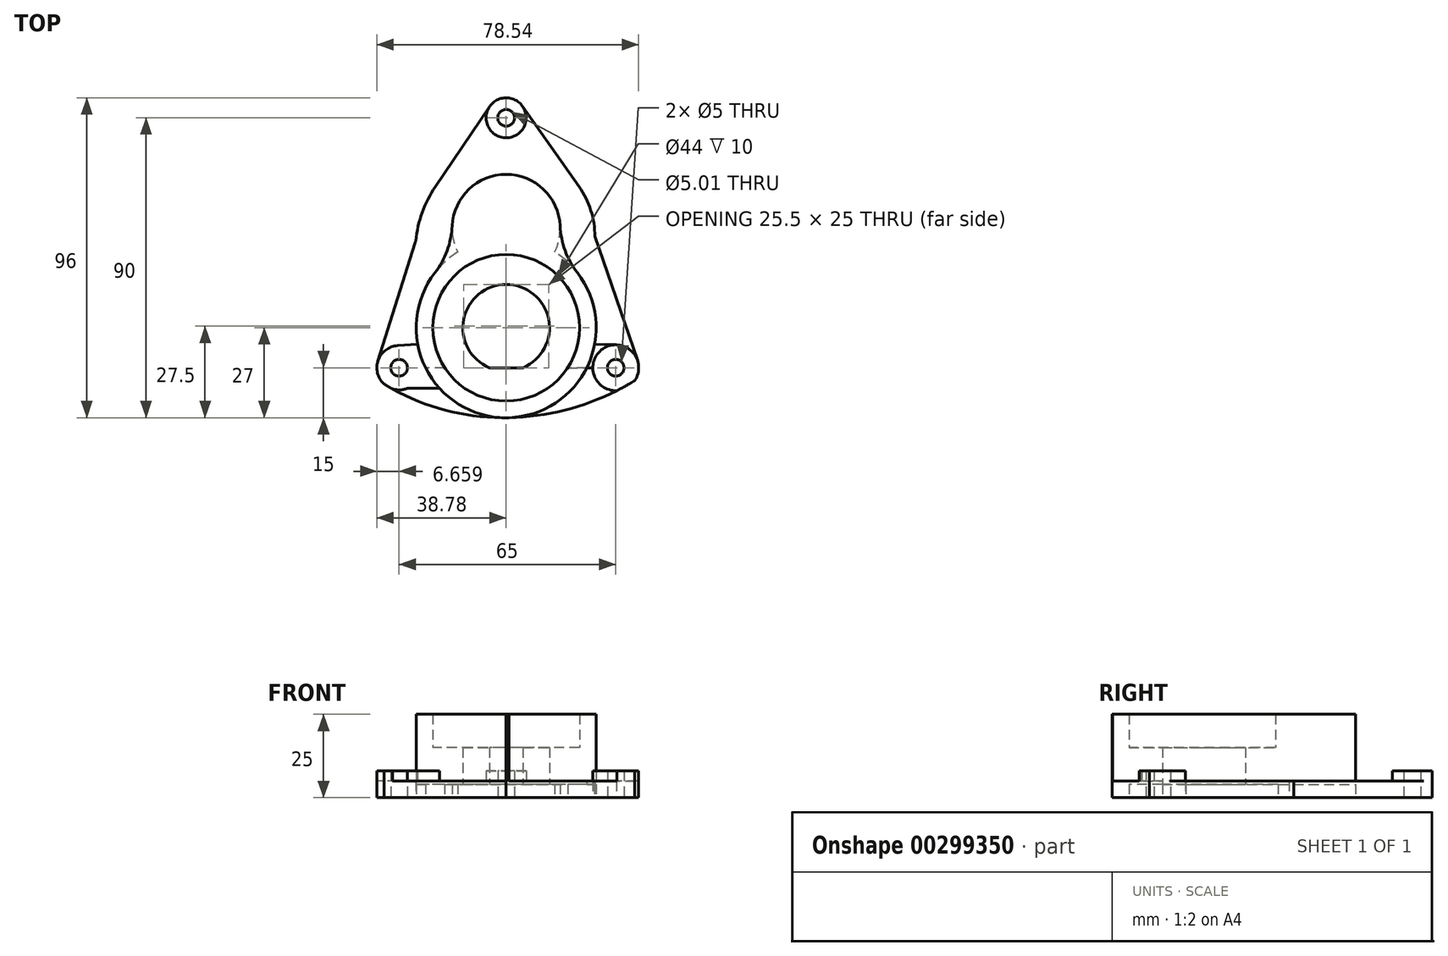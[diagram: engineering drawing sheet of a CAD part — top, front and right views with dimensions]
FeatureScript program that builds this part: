
annotation { "Feature Type Name" : "Feature", "Feature Type Description" : "" }
export const myFeature = defineFeature(function(context is Context, id is Id, definition is map)
    precondition{}
    {
        {
            var Q0;
            Q0=qCreatedBy(makeId("Top.planeOp"),FACE);
            var sketch = newSketch(context, id + "F0", { "sketchPlane" : qUnion([Q0])});
            skCircle(sketch, "E0", {"center": v(0, 0) * mm, "radius": 13 * mm});
            skCircle(sketch, "E1", {"center": v(0, 0) * mm, "radius": 22 * mm});
            skCircle(sketch, "E2", {"center": v(0, 0) * mm, "radius": 27 * mm});
            skLineSegment(sketch, "E3", {"start": v(-99.8, -12) * mm, "end": v(99.48, -12) * mm});
            skCircle(sketch, "E4", {"center": v(32.88, -12) * mm, "radius": 2.5 * mm});
            skCircle(sketch, "E5", {"center": v(32.88, -12) * mm, "radius": 6.88 * mm});
            skCircle(sketch, "E6", {"center": v(-32.12, -12) * mm, "radius": 2.5 * mm});
            skCircle(sketch, "E7", {"center": v(-32.12, -12) * mm, "radius": 6.66 * mm});
            skCircle(sketch, "E8", {"center": v(0, 29.79) * mm, "radius": 11.21 * mm});
            skArc(sketch, "E9", {"start": v(14.59, 22.72) * mm, "mid": v(0, 46) * mm, "end": v(-14.59, 22.72) * mm});
            skCircle(sketch, "E10", {"center": v(0, 63) * mm, "radius": 6 * mm});
            skCircle(sketch, "E11", {"center": v(0, 63) * mm, "radius": 2.5 * mm});
            skLineSegment(sketch, "E12", {"start": v(-32.55, -5.36) * mm, "end": v(-26.54, -4.97) * mm});
            skLineSegment(sketch, "E13", {"start": v(-34.56, -18.2) * mm, "end": v(-19.95, -18.2) * mm});
            skLineSegment(sketch, "E14", {"start": v(33.04, -5.12) * mm, "end": v(26.54, -4.97) * mm});
            skLineSegment(sketch, "E15", {"start": v(33.32, -18.87) * mm, "end": v(19.62, -18.55) * mm});
            skLineSegment(sketch, "E16", {"start": v(-27.35, 25.47) * mm, "end": v(-39.1, -12) * mm});
            skLineSegment(sketch, "E17", {"start": v(26.61, 27.38) * mm, "end": v(40.16, -12) * mm});
            skArc(sketch, "E18", {"start": v(0, -27) * mm, "mid": v(20.05, -24.05) * mm, "end": v(38.58, -15.85) * mm});
            skArc(sketch, "E19", {"start": v(-36.68, -16.85) * mm, "mid": v(-19.05, -24.5) * mm, "end": v(0, -27) * mm});
            skLineSegment(sketch, "E20", {"start": v(0, -27) * mm, "end": v(-95.56, -27) * mm});
            skLineSegment(sketch, "E21", {"start": v(-21.25, 42.32) * mm, "end": v(-4.97, 66.36) * mm});
            skLineSegment(sketch, "E22", {"start": v(21.9, 42.32) * mm, "end": v(4.9, 66.45) * mm});
            skLineSegment(sketch, "E23", {"start": v(4.1, 45.47) * mm, "end": v(2.99, 57.8) * mm});
            skLineSegment(sketch, "E24", {"start": v(-4.1, 45.47) * mm, "end": v(-2.99, 57.8) * mm});
            skPoint(sketch, "E25.visualSharp", {"position": v(-26.96, 26.7) * mm});
            skArc(sketch, "E25.filletArc", {"start": v(-27.1, 26.1) * mm, "mid": v(-27.24, 25.78) * mm, "end": v(-27.35, 25.47) * mm});
            skPoint(sketch, "E26.visualSharp", {"position": v(26.2, 28.55) * mm});
            skArc(sketch, "E27", {"start": v(-21.25, 42.32) * mm, "mid": v(-25.2, 34.57) * mm, "end": v(-27.1, 26.1) * mm});
            skArc(sketch, "E28", {"start": v(21.9, 42.32) * mm, "mid": v(25.41, 35.21) * mm, "end": v(26.61, 27.38) * mm});
            skSolve(sketch);
        }
        {
            var Q0;
            {var subQ1=sQuery(id+"F0.wireOp",EDGE,"E2");var subQ4=sQuery(id+"F0.wireOp",EDGE,"E9");var subQ6=makeQuery(id+"F0.imprint","INTERSECT",VERTEX,{"disambiguationData":[OD(0.0)],"derivedFrom":[subQ1,subQ4]});Q0=makeQuery(id+"F0.imprint","IMPRINT",FACE,{"disambiguationData":[TD([[makeQuery(id+"F0.imprint","IMPRINT",EDGE,{"disambiguationData":[TD([[subQ6,-1.0]])],"derivedFrom":subQ1}),-1.0]])]});}
            var Q1;
            {var subQ1=sQuery(id+"F0.wireOp",EDGE,"E1");var subQ6=sQuery(id+"F0.wireOp",EDGE,"E8");var subQ7=makeQuery(id+"F0.imprint","INTERSECT",VERTEX,{"disambiguationData":[OD(1.0)],"derivedFrom":[subQ1,subQ6]});Q1=makeQuery(id+"F0.imprint","IMPRINT",FACE,{"disambiguationData":[TD([[makeQuery(id+"F0.imprint","IMPRINT",EDGE,{"disambiguationData":[TD([[subQ7,1.0]])],"derivedFrom":subQ1}),-1.0]])]});}
            var Q2;
            {var subQ5=sQuery(id+"F0.wireOp",EDGE,"E8");var subQ7=sQuery(id+"F0.wireOp",EDGE,"E1");var subQ8=makeQuery(id+"F0.imprint","INTERSECT",VERTEX,{"disambiguationData":[OD(0.0)],"derivedFrom":[subQ7,subQ5]});Q2=makeQuery(id+"F0.imprint","IMPRINT",FACE,{"disambiguationData":[TD([[makeQuery(id+"F0.imprint","IMPRINT",EDGE,{"disambiguationData":[TD([[subQ8,-1.0]])],"derivedFrom":subQ7}),-1.0]])]});}
            var Q3;
            {var subQ4=sQuery(id+"F0.wireOp",EDGE,"E3");var subQ6=sQuery(id+"F0.wireOp",EDGE,"E1");var subQ7=makeQuery(id+"F0.imprint","INTERSECT",VERTEX,{"disambiguationData":[OD(0.0)],"derivedFrom":[subQ6,subQ4]});Q3=makeQuery(id+"F0.imprint","IMPRINT",FACE,{"disambiguationData":[TD([[makeQuery(id+"F0.imprint","IMPRINT",EDGE,{"disambiguationData":[TD([[subQ7,-1.0]])],"derivedFrom":subQ6}),-1.0]])]});}
            extrude(context, id + "F1", {"entities" : qUnion([Q0, Q1, Q2, Q3]), "depth" : 25 * mm});
        }
        {
            var Q0;
            {var subQ3=sQuery(id+"F0.wireOp",EDGE,"E3");var subQ5=sQuery(id+"F0.wireOp",EDGE,"E0");var subQ6=makeQuery(id+"F0.imprint","INTERSECT",VERTEX,{"disambiguationData":[OD(0.0)],"derivedFrom":[subQ5,subQ3]});Q0=makeQuery(id+"F0.imprint","IMPRINT",FACE,{"disambiguationData":[TD([[makeQuery(id+"F0.imprint","IMPRINT",EDGE,{"disambiguationData":[TD([[subQ6,1.0]])],"derivedFrom":subQ5}),-1.0]])]});}
            var Q1;
            {var subQ0=sQuery(id+"F0.wireOp",EDGE,"E3");var subQ1=sQuery(id+"F0.wireOp",EDGE,"E0");var subQ2=makeQuery(id+"F0.imprint","INTERSECT",VERTEX,{"disambiguationData":[OD(0.0)],"derivedFrom":[subQ1,subQ0]});Q1=makeQuery(id+"F0.imprint","IMPRINT",FACE,{"disambiguationData":[TD([[makeQuery(id+"F0.imprint","IMPRINT",EDGE,{"disambiguationData":[TD([[subQ2,1.0]])],"derivedFrom":subQ1}),1.0]])]});}
            var Q2;
            {var subQ0=sQuery(id+"F0.wireOp",EDGE,"E3");var subQ1=sQuery(id+"F0.wireOp",EDGE,"E0");var subQ2=makeQuery(id+"F0.imprint","INTERSECT",VERTEX,{"disambiguationData":[OD(0.0)],"derivedFrom":[subQ1,subQ0]});Q2=makeQuery(id+"F0.imprint","IMPRINT",FACE,{"disambiguationData":[TD([[makeQuery(id+"F0.imprint","IMPRINT",EDGE,{"disambiguationData":[TD([[subQ2,-1.0]])],"derivedFrom":subQ1}),-1.0]])]});}
            var Q3;
            {var subQ0=sQuery(id+"F0.wireOp",EDGE,"E8");var subQ1=sQuery(id+"F0.wireOp",EDGE,"E1");var subQ2=makeQuery(id+"F0.imprint","INTERSECT",VERTEX,{"disambiguationData":[OD(0.0)],"derivedFrom":[subQ1,subQ0]});Q3=makeQuery(id+"F0.imprint","IMPRINT",FACE,{"disambiguationData":[TD([[makeQuery(id+"F0.imprint","IMPRINT",EDGE,{"disambiguationData":[TD([[subQ2,1.0]])],"derivedFrom":subQ1}),1.0]])]});}
            var Q4;
            {var subQ0=sQuery(id+"F0.wireOp",EDGE,"E3");var subQ1=sQuery(id+"F0.wireOp",EDGE,"E0");var subQ2=makeQuery(id+"F0.imprint","INTERSECT",VERTEX,{"disambiguationData":[OD(0.0)],"derivedFrom":[subQ1,subQ0]});Q4=makeQuery(id+"F0.imprint","IMPRINT",FACE,{"disambiguationData":[TD([[makeQuery(id+"F0.imprint","IMPRINT",EDGE,{"disambiguationData":[TD([[subQ2,-1.0]])],"derivedFrom":subQ1}),1.0]])]});}
            extrude(context, id + "F2", {"entities" : qUnion([Q0, Q1, Q2, Q3, Q4]), "operationType" : NewBodyOperationType.ADD, "depth" : 15 * mm});
        }
        {
            var Q0;
            {var subQ0=sQuery(id+"F0.wireOp",EDGE,"E8");var subQ1=sQuery(id+"F0.wireOp",EDGE,"E2");var subQ2=makeQuery(id+"F0.imprint","INTERSECT",VERTEX,{"disambiguationData":[OD(0.0)],"derivedFrom":[subQ1,subQ0]});Q0=makeQuery(id+"F0.imprint","IMPRINT",FACE,{"disambiguationData":[TD([[makeQuery(id+"F0.imprint","IMPRINT",EDGE,{"disambiguationData":[TD([[subQ2,-1.0]])],"derivedFrom":subQ1}),-1.0]])]});}
            var Q1;
            {var subQ0=sQuery(id+"F0.wireOp",EDGE,"E8");var subQ1=sQuery(id+"F0.wireOp",EDGE,"E1");var subQ2=makeQuery(id+"F0.imprint","INTERSECT",VERTEX,{"disambiguationData":[OD(0.0)],"derivedFrom":[subQ1,subQ0]});Q1=makeQuery(id+"F0.imprint","IMPRINT",FACE,{"disambiguationData":[TD([[makeQuery(id+"F0.imprint","IMPRINT",EDGE,{"disambiguationData":[TD([[subQ2,1.0]])],"derivedFrom":subQ1}),-1.0]])]});}
            extrude(context, id + "F3", {"entities" : qUnion([Q0, Q1]), "operationType" : NewBodyOperationType.ADD, "depth" : 25 * mm});
        }
        {
            var Q0;
            {var subQ6=sQuery(id+"F0.wireOp",EDGE,"E12");Q0=makeQuery(id+"F0.imprint","IMPRINT",FACE,{"disambiguationData":[TD([[makeQuery(id+"F0.imprint","IMPRINT",EDGE,{"derivedFrom":subQ6}),1.0]])]});}
            var Q1;
            {var subQ0=sQuery(id+"F0.wireOp",EDGE,"E12");Q1=makeQuery(id+"F0.imprint","IMPRINT",FACE,{"disambiguationData":[TD([[makeQuery(id+"F0.imprint","IMPRINT",EDGE,{"derivedFrom":subQ0}),-1.0]])]});}
            var Q2;
            {var subQ0=sQuery(id+"F0.wireOp",EDGE,"E13");var subQ1=sQuery(id+"F0.wireOp",EDGE,"E2");var subQ2=makeQuery(id+"F0.imprint","INTERSECT",VERTEX,{"derivedFrom":[subQ1,subQ0]});Q2=makeQuery(id+"F0.imprint","IMPRINT",FACE,{"disambiguationData":[TD([[makeQuery(id+"F0.imprint","IMPRINT",EDGE,{"disambiguationData":[TD([[subQ2,1.0]])],"derivedFrom":subQ1}),-1.0]])]});}
            var Q3;
            {var subQ1=sQuery(id+"F0.wireOp",EDGE,"E19");var subQ3=sQuery(id+"F0.wireOp",EDGE,"E7");var subQ4=makeQuery(id+"F0.imprint","INTERSECT",VERTEX,{"disambiguationData":[OD(1.0)],"derivedFrom":[subQ3,subQ1]});Q3=makeQuery(id+"F0.imprint","IMPRINT",FACE,{"disambiguationData":[TD([[makeQuery(id+"F0.imprint","IMPRINT",EDGE,{"disambiguationData":[TD([[subQ4,-1.0]])],"derivedFrom":subQ3}),-1.0]])]});}
            var Q4;
            {var subQ0=sQuery(id+"F0.wireOp",EDGE,"E15");var subQ4=sQuery(id+"F0.wireOp",EDGE,"E2");var subQ5=makeQuery(id+"F0.imprint","INTERSECT",VERTEX,{"derivedFrom":[subQ4,subQ0]});Q4=makeQuery(id+"F0.imprint","IMPRINT",FACE,{"disambiguationData":[TD([[makeQuery(id+"F0.imprint","IMPRINT",EDGE,{"disambiguationData":[TD([[subQ5,1.0]])],"derivedFrom":subQ4}),-1.0]])]});}
            var Q5;
            {var subQ0=sQuery(id+"F0.wireOp",EDGE,"E15");var subQ1=sQuery(id+"F0.wireOp",EDGE,"E2");var subQ2=makeQuery(id+"F0.imprint","INTERSECT",VERTEX,{"derivedFrom":[subQ1,subQ0]});Q5=makeQuery(id+"F0.imprint","IMPRINT",FACE,{"disambiguationData":[TD([[makeQuery(id+"F0.imprint","IMPRINT",EDGE,{"disambiguationData":[TD([[subQ2,-1.0]])],"derivedFrom":subQ1}),-1.0]])]});}
            var Q6;
            {var subQ11=sQuery(id+"F0.wireOp",EDGE,"E22");Q6=makeQuery(id+"F0.imprint","IMPRINT",FACE,{"disambiguationData":[TD([[makeQuery(id+"F0.imprint","IMPRINT",EDGE,{"derivedFrom":subQ11}),1.0]])]});}
            var Q7;
            {var subQ0=sQuery(id+"F0.wireOp",EDGE,"E23");Q7=makeQuery(id+"F0.imprint","IMPRINT",FACE,{"disambiguationData":[TD([[makeQuery(id+"F0.imprint","IMPRINT",EDGE,{"derivedFrom":subQ0}),1.0]])]});}
            var Q8;
            {var subQ0=sQuery(id+"F0.wireOp",EDGE,"E21");Q8=makeQuery(id+"F0.imprint","IMPRINT",FACE,{"disambiguationData":[TD([[makeQuery(id+"F0.imprint","IMPRINT",EDGE,{"derivedFrom":subQ0}),-1.0]])]});}
            var Q9;
            {var subQ0=sQuery(id+"F0.wireOp",EDGE,"E15");var subQ1=sQuery(id+"F0.wireOp",EDGE,"E2");var subQ2=makeQuery(id+"F0.imprint","INTERSECT",VERTEX,{"derivedFrom":[subQ1,subQ0]});Q9=makeQuery(id+"F0.imprint","IMPRINT",FACE,{"disambiguationData":[TD([[makeQuery(id+"F0.imprint","IMPRINT",EDGE,{"disambiguationData":[TD([[subQ2,1.0]])],"derivedFrom":subQ1}),-1.0]])]});}
            extrude(context, id + "F4", {"entities" : qUnion([Q0, Q1, Q2, Q3, Q4, Q5, Q6, Q7, Q8, Q9]), "operationType" : NewBodyOperationType.ADD, "depth" : 5 * mm});
        }
        {
            var Q0;
            {var subQ0=sQuery(id+"F0.wireOp",EDGE,"E7");var subQ4=sQuery(id+"F0.wireOp",EDGE,"E3");var subQ8=makeQuery(id+"F0.imprint","INTERSECT",VERTEX,{"disambiguationData":[OD(0.0)],"derivedFrom":[subQ4,subQ0]});Q0=makeQuery(id+"F0.imprint","IMPRINT",FACE,{"disambiguationData":[TD([[makeQuery(id+"F0.imprint","IMPRINT",EDGE,{"disambiguationData":[TD([[subQ8,-1.0]])],"derivedFrom":subQ4}),1.0]])]});}
            var Q1;
            {var subQ1=sQuery(id+"F0.wireOp",EDGE,"E7");var subQ3=sQuery(id+"F0.wireOp",EDGE,"E3");var subQ4=makeQuery(id+"F0.imprint","INTERSECT",VERTEX,{"disambiguationData":[OD(0.0)],"derivedFrom":[subQ3,subQ1]});Q1=makeQuery(id+"F0.imprint","IMPRINT",FACE,{"disambiguationData":[TD([[makeQuery(id+"F0.imprint","IMPRINT",EDGE,{"disambiguationData":[TD([[subQ4,-1.0]])],"derivedFrom":subQ3}),-1.0]])]});}
            var Q2;
            {var subQ0=sQuery(id+"F0.wireOp",EDGE,"E19");var subQ1=sQuery(id+"F0.wireOp",EDGE,"E7");var subQ2=makeQuery(id+"F0.imprint","INTERSECT",VERTEX,{"disambiguationData":[OD(1.0)],"derivedFrom":[subQ1,subQ0]});Q2=makeQuery(id+"F0.imprint","IMPRINT",FACE,{"disambiguationData":[TD([[makeQuery(id+"F0.imprint","IMPRINT",EDGE,{"disambiguationData":[TD([[subQ2,-1.0]])],"derivedFrom":subQ1}),1.0]])]});}
            var Q3;
            {var subQ0=sQuery(id+"F0.wireOp",EDGE,"E13");var subQ1=sQuery(id+"F0.wireOp",EDGE,"E7");var subQ2=makeQuery(id+"F0.imprint","INTERSECT",VERTEX,{"disambiguationData":[OD(0.0)],"derivedFrom":[subQ1,subQ0]});Q3=makeQuery(id+"F0.imprint","IMPRINT",FACE,{"disambiguationData":[TD([[makeQuery(id+"F0.imprint","IMPRINT",EDGE,{"disambiguationData":[TD([[subQ2,1.0]])],"derivedFrom":subQ1}),1.0]])]});}
            var Q4;
            {var subQ0=sQuery(id+"F0.wireOp",EDGE,"E13");var subQ1=sQuery(id+"F0.wireOp",EDGE,"E7");var subQ2=makeQuery(id+"F0.imprint","INTERSECT",VERTEX,{"disambiguationData":[OD(0.0)],"derivedFrom":[subQ1,subQ0]});Q4=makeQuery(id+"F0.imprint","IMPRINT",FACE,{"disambiguationData":[TD([[makeQuery(id+"F0.imprint","IMPRINT",EDGE,{"disambiguationData":[TD([[subQ2,-1.0]])],"derivedFrom":subQ1}),1.0]])]});}
            var Q5;
            {var subQ0=sQuery(id+"F0.wireOp",EDGE,"E5");var subQ1=sQuery(id+"F0.wireOp",EDGE,"E3");var subQ2=makeQuery(id+"F0.imprint","INTERSECT",VERTEX,{"disambiguationData":[OD(1.0)],"derivedFrom":[subQ1,subQ0]});Q5=makeQuery(id+"F0.imprint","IMPRINT",FACE,{"disambiguationData":[TD([[makeQuery(id+"F0.imprint","IMPRINT",EDGE,{"disambiguationData":[TD([[subQ2,-1.0]])],"derivedFrom":subQ1}),-1.0]])]});}
            var Q6;
            {var subQ0=sQuery(id+"F0.wireOp",EDGE,"E5");var subQ8=makeQuery(id+"F0.imprint","IMPRINT",VERTEX,{"derivedFrom":subQ0});Q6=makeQuery(id+"F0.imprint","IMPRINT",FACE,{"disambiguationData":[TD([[makeQuery(id+"F0.imprint","IMPRINT",EDGE,{"disambiguationData":[TD([[subQ8,1.0]])],"derivedFrom":subQ0}),1.0]])]});}
            var Q7;
            {var subQ0=sQuery(id+"F0.wireOp",EDGE,"E18");var subQ1=sQuery(id+"F0.wireOp",EDGE,"E5");var subQ2=makeQuery(id+"F0.imprint","INTERSECT",VERTEX,{"disambiguationData":[OD(0.0)],"derivedFrom":[subQ1,subQ0]});Q7=makeQuery(id+"F0.imprint","IMPRINT",FACE,{"disambiguationData":[TD([[makeQuery(id+"F0.imprint","IMPRINT",EDGE,{"disambiguationData":[TD([[subQ2,1.0]])],"derivedFrom":subQ1}),1.0]])]});}
            var Q8;
            Q8=makeQuery(id+"F0.imprint","IMPRINT",FACE,{"disambiguationData":[TD([[makeQuery(id+"F0.imprint","IMPRINT",EDGE,{"derivedFrom":sQuery(id+"F0.wireOp",EDGE,"E11")}),-1.0]])]});
            var Q9;
            {var subQ0=sQuery(id+"F0.wireOp",EDGE,"E13");var subQ1=sQuery(id+"F0.wireOp",EDGE,"E2");var subQ2=makeQuery(id+"F0.imprint","INTERSECT",VERTEX,{"derivedFrom":[subQ1,subQ0]});Q9=makeQuery(id+"F0.imprint","IMPRINT",FACE,{"disambiguationData":[TD([[makeQuery(id+"F0.imprint","IMPRINT",EDGE,{"disambiguationData":[TD([[subQ2,1.0]])],"derivedFrom":subQ1}),-1.0]])]});}
            var Q10;
            {var subQ0=sQuery(id+"F0.wireOp",EDGE,"E12");Q10=makeQuery(id+"F0.imprint","IMPRINT",FACE,{"disambiguationData":[TD([[makeQuery(id+"F0.imprint","IMPRINT",EDGE,{"derivedFrom":subQ0}),-1.0]])]});}
            var Q11;
            {var subQ0=sQuery(id+"F0.wireOp",EDGE,"E15");var subQ1=sQuery(id+"F0.wireOp",EDGE,"E2");var subQ2=makeQuery(id+"F0.imprint","INTERSECT",VERTEX,{"derivedFrom":[subQ1,subQ0]});Q11=makeQuery(id+"F0.imprint","IMPRINT",FACE,{"disambiguationData":[TD([[makeQuery(id+"F0.imprint","IMPRINT",EDGE,{"disambiguationData":[TD([[subQ2,-1.0]])],"derivedFrom":subQ1}),-1.0]])]});}
            var Q12;
            {var subQ0=sQuery(id+"F0.wireOp",EDGE,"E14");Q12=makeQuery(id+"F0.imprint","IMPRINT",FACE,{"disambiguationData":[TD([[makeQuery(id+"F0.imprint","IMPRINT",EDGE,{"derivedFrom":subQ0}),1.0]])]});}
            var Q13;
            {var subQ0=sQuery(id+"F0.wireOp",EDGE,"E5");var subQ1=sQuery(id+"F0.wireOp",EDGE,"E3");var subQ7=makeQuery(id+"F0.imprint","INTERSECT",VERTEX,{"disambiguationData":[OD(1.0)],"derivedFrom":[subQ1,subQ0]});Q13=makeQuery(id+"F0.imprint","IMPRINT",FACE,{"disambiguationData":[TD([[makeQuery(id+"F0.imprint","IMPRINT",EDGE,{"disambiguationData":[TD([[subQ7,-1.0]])],"derivedFrom":subQ1}),1.0]])]});}
            extrude(context, id + "F5", {"entities" : qUnion([Q0, Q1, Q2, Q3, Q4, Q5, Q6, Q7, Q8, Q9, Q10, Q11, Q12, Q13]), "operationType" : NewBodyOperationType.ADD, "depth" : 8 * mm});
        }
        {
            var Q0;
            {var subQ0=sQuery(id+"F0.wireOp",EDGE,"E9");var subQ1=sQuery(id+"F0.wireOp",EDGE,"E2");Q0=makeQuery(id+"F1.opExtrude","SWEPT_EDGE",EDGE,{"disambiguationData":[OSD([subQ1,subQ0]),TDD([makeQuery(id+"F0.imprint","INTERSECT",VERTEX,{"disambiguationData":[OD(0.0)],"derivedFrom":[subQ1,subQ0]})])]});}
            var Q1;
            {var subQ0=sQuery(id+"F0.wireOp",EDGE,"E9");var subQ1=sQuery(id+"F0.wireOp",EDGE,"E2");Q1=makeQuery(id+"F1.opExtrude","SWEPT_EDGE",EDGE,{"disambiguationData":[OSD([subQ1,subQ0]),TDD([makeQuery(id+"F0.imprint","INTERSECT",VERTEX,{"disambiguationData":[OD(1.0)],"derivedFrom":[subQ1,subQ0]})])]});}
            fillet(context, id + "F6", {"entities" : qUnion([Q0, Q1]), "radius" : 25 * mm, "tangentPropagation" : true, "allowEdgeOverflow" : false});
        }
        {
            var Q0;
            {var subQ0=sQuery(id+"F0.wireOp",EDGE,"E3");var subQ1=sQuery(id+"F0.wireOp",EDGE,"E0");var subQ2=makeQuery(id+"F0.imprint","INTERSECT",VERTEX,{"disambiguationData":[OD(0.0)],"derivedFrom":[subQ1,subQ0]});Q0=makeQuery(id+"F0.imprint","IMPRINT",FACE,{"disambiguationData":[TD([[makeQuery(id+"F0.imprint","IMPRINT",EDGE,{"disambiguationData":[TD([[subQ2,1.0]])],"derivedFrom":subQ1}),1.0]])]});}
            var Q1;
            {var subQ0=sQuery(id+"F0.wireOp",EDGE,"E3");var subQ1=sQuery(id+"F0.wireOp",EDGE,"E0");var subQ2=makeQuery(id+"F0.imprint","INTERSECT",VERTEX,{"disambiguationData":[OD(0.0)],"derivedFrom":[subQ1,subQ0]});Q1=makeQuery(id+"F0.imprint","IMPRINT",FACE,{"disambiguationData":[TD([[makeQuery(id+"F0.imprint","IMPRINT",EDGE,{"disambiguationData":[TD([[subQ2,1.0]])],"derivedFrom":subQ1}),-1.0]])]});}
            var Q2;
            {var subQ0=sQuery(id+"F0.wireOp",EDGE,"E3");var subQ1=sQuery(id+"F0.wireOp",EDGE,"E0");var subQ2=makeQuery(id+"F0.imprint","INTERSECT",VERTEX,{"disambiguationData":[OD(0.0)],"derivedFrom":[subQ1,subQ0]});Q2=makeQuery(id+"F0.imprint","IMPRINT",FACE,{"disambiguationData":[TD([[makeQuery(id+"F0.imprint","IMPRINT",EDGE,{"disambiguationData":[TD([[subQ2,-1.0]])],"derivedFrom":subQ1}),-1.0]])]});}
            var Q3;
            {var subQ0=sQuery(id+"F0.wireOp",EDGE,"E3");var subQ1=sQuery(id+"F0.wireOp",EDGE,"E0");var subQ2=makeQuery(id+"F0.imprint","INTERSECT",VERTEX,{"disambiguationData":[OD(0.0)],"derivedFrom":[subQ1,subQ0]});Q3=makeQuery(id+"F0.imprint","IMPRINT",FACE,{"disambiguationData":[TD([[makeQuery(id+"F0.imprint","IMPRINT",EDGE,{"disambiguationData":[TD([[subQ2,-1.0]])],"derivedFrom":subQ1}),1.0]])]});}
            var Q4;
            {var subQ0=sQuery(id+"F0.wireOp",EDGE,"E8");var subQ1=sQuery(id+"F0.wireOp",EDGE,"E1");var subQ2=makeQuery(id+"F0.imprint","INTERSECT",VERTEX,{"disambiguationData":[OD(0.0)],"derivedFrom":[subQ1,subQ0]});Q4=makeQuery(id+"F0.imprint","IMPRINT",FACE,{"disambiguationData":[TD([[makeQuery(id+"F0.imprint","IMPRINT",EDGE,{"disambiguationData":[TD([[subQ2,1.0]])],"derivedFrom":subQ1}),1.0]])]});}
            var Q5;
            {var subQ0=sQuery(id+"F0.wireOp",EDGE,"E8");var subQ1=sQuery(id+"F0.wireOp",EDGE,"E1");var subQ2=makeQuery(id+"F0.imprint","INTERSECT",VERTEX,{"disambiguationData":[OD(0.0)],"derivedFrom":[subQ1,subQ0]});Q5=makeQuery(id+"F0.imprint","IMPRINT",FACE,{"disambiguationData":[TD([[makeQuery(id+"F0.imprint","IMPRINT",EDGE,{"disambiguationData":[TD([[subQ2,1.0]])],"derivedFrom":subQ1}),-1.0]])]});}
            var Q6;
            {var subQ0=sQuery(id+"F0.wireOp",EDGE,"E8");var subQ1=sQuery(id+"F0.wireOp",EDGE,"E2");var subQ2=makeQuery(id+"F0.imprint","INTERSECT",VERTEX,{"disambiguationData":[OD(0.0)],"derivedFrom":[subQ1,subQ0]});Q6=makeQuery(id+"F0.imprint","IMPRINT",FACE,{"disambiguationData":[TD([[makeQuery(id+"F0.imprint","IMPRINT",EDGE,{"disambiguationData":[TD([[subQ2,-1.0]])],"derivedFrom":subQ1}),-1.0]])]});}
            var Q7;
            {var subQ0=sQuery(id+"F0.wireOp",EDGE,"E9");var subQ1=sQuery(id+"F0.wireOp",EDGE,"E2");var subQ2=makeQuery(id+"F0.imprint","INTERSECT",VERTEX,{"disambiguationData":[OD(0.0)],"derivedFrom":[subQ1,subQ0]});Q7=makeQuery(id+"F0.imprint","IMPRINT",FACE,{"disambiguationData":[TD([[makeQuery(id+"F0.imprint","IMPRINT",EDGE,{"disambiguationData":[TD([[subQ2,-1.0]])],"derivedFrom":subQ1}),-1.0]])]});}
            var Q8;
            {var subQ5=sQuery(id+"F0.wireOp",EDGE,"E8");var subQ6=sQuery(id+"F0.wireOp",EDGE,"E1");var subQ7=makeQuery(id+"F0.imprint","INTERSECT",VERTEX,{"disambiguationData":[OD(0.0)],"derivedFrom":[subQ6,subQ5]});Q8=makeQuery(id+"F0.imprint","IMPRINT",FACE,{"disambiguationData":[TD([[makeQuery(id+"F0.imprint","IMPRINT",EDGE,{"disambiguationData":[TD([[subQ7,-1.0]])],"derivedFrom":subQ6}),-1.0]])]});}
            var Q9;
            {var subQ4=sQuery(id+"F0.wireOp",EDGE,"E3");var subQ5=sQuery(id+"F0.wireOp",EDGE,"E1");var subQ6=makeQuery(id+"F0.imprint","INTERSECT",VERTEX,{"disambiguationData":[OD(0.0)],"derivedFrom":[subQ5,subQ4]});Q9=makeQuery(id+"F0.imprint","IMPRINT",FACE,{"disambiguationData":[TD([[makeQuery(id+"F0.imprint","IMPRINT",EDGE,{"disambiguationData":[TD([[subQ6,-1.0]])],"derivedFrom":subQ5}),-1.0]])]});}
            var Q10;
            {var subQ3=sQuery(id+"F0.wireOp",EDGE,"E8");var subQ7=sQuery(id+"F0.wireOp",EDGE,"E1");var subQ8=makeQuery(id+"F0.imprint","INTERSECT",VERTEX,{"disambiguationData":[OD(1.0)],"derivedFrom":[subQ7,subQ3]});Q10=makeQuery(id+"F0.imprint","IMPRINT",FACE,{"disambiguationData":[TD([[makeQuery(id+"F0.imprint","IMPRINT",EDGE,{"disambiguationData":[TD([[subQ8,1.0]])],"derivedFrom":subQ7}),-1.0]])]});}
            extrude(context, id + "F7", {"entities" : qUnion([Q0, Q1, Q2, Q3, Q4, Q5, Q6, Q7, Q8, Q9, Q10]), "operationType" : NewBodyOperationType.REMOVE, "depth" : 4 * mm});
        }
        {
            var Q0;
            {var subQ0=sQuery(id+"F0.wireOp",EDGE,"E3");var subQ1=sQuery(id+"F0.wireOp",EDGE,"E0");var subQ2=makeQuery(id+"F0.imprint","INTERSECT",VERTEX,{"disambiguationData":[OD(0.0)],"derivedFrom":[subQ1,subQ0]});Q0=makeQuery(id+"F0.imprint","IMPRINT",FACE,{"disambiguationData":[TD([[makeQuery(id+"F0.imprint","IMPRINT",EDGE,{"disambiguationData":[TD([[subQ2,1.0]])],"derivedFrom":subQ1}),1.0]])]});}
            extrude(context, id + "F8", {"entities" : qUnion([Q0]), "operationType" : NewBodyOperationType.REMOVE, "endBound" : BoundingType.THROUGH_ALL, "depth" : 25 * mm});
        }
        {
            var Q0;
            {var subQ4=sQuery(id+"F0.wireOp",EDGE,"E3");var subQ5=sQuery(id+"F0.wireOp",EDGE,"E1");var subQ6=makeQuery(id+"F0.imprint","INTERSECT",VERTEX,{"disambiguationData":[OD(0.0)],"derivedFrom":[subQ5,subQ4]});Q0=makeQuery(id+"F0.imprint","IMPRINT",FACE,{"disambiguationData":[TD([[makeQuery(id+"F0.imprint","IMPRINT",EDGE,{"disambiguationData":[TD([[subQ6,-1.0]])],"derivedFrom":subQ5}),-1.0]])]});}
            extrude(context, id + "F9", {"entities" : qUnion([Q0]), "operationType" : NewBodyOperationType.ADD, "depth" : 25 * mm});
        }
    });
